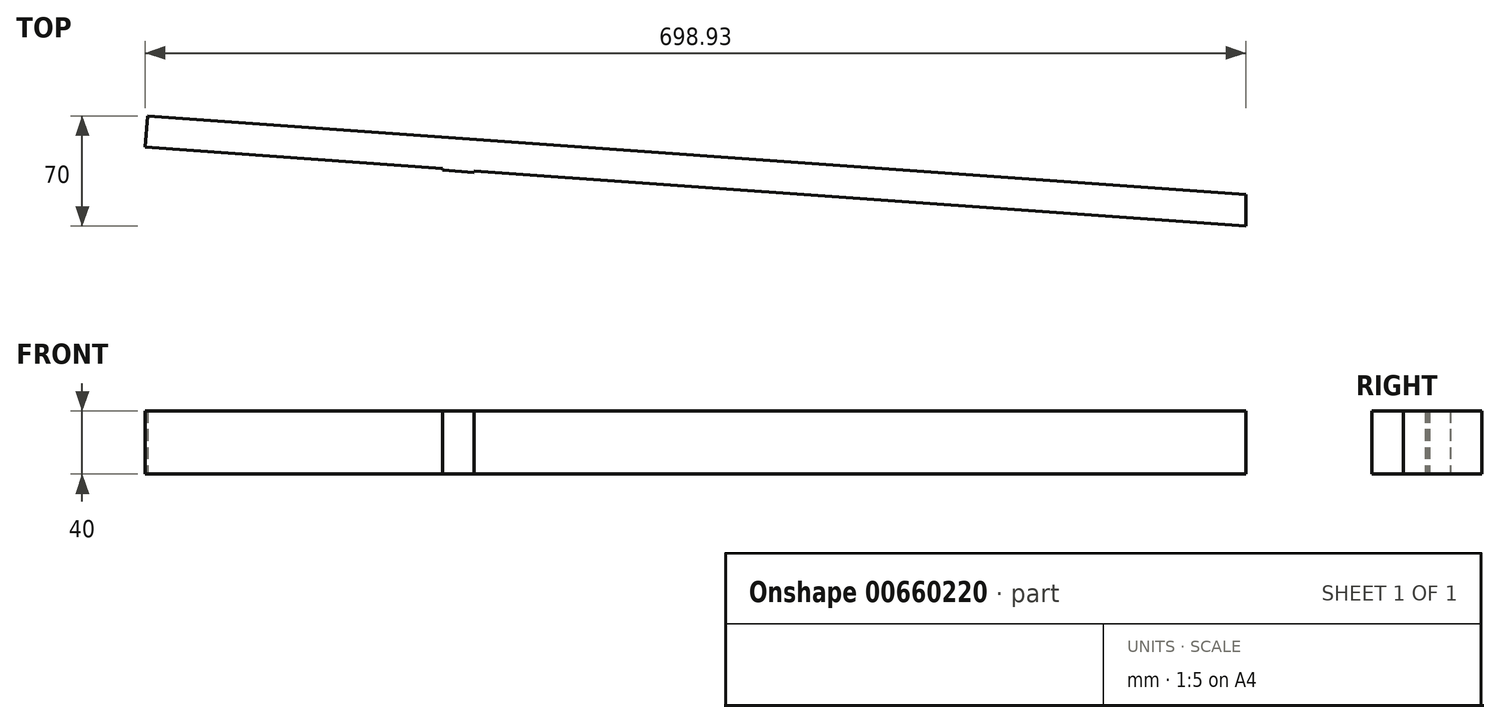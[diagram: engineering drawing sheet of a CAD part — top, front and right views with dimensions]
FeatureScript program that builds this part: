
annotation { "Feature Type Name" : "Feature", "Feature Type Description" : "" }
export const myFeature = defineFeature(function(context is Context, id is Id, definition is map)
    precondition{}
    {
        {
            var Q0;
            Q0=qCreatedBy(makeId("Top.planeOp"),FACE);
            var sketch = newSketch(context, id + "F0", { "sketchPlane" : qUnion([Q0])});
            skLineSegment(sketch, "E0", {"start": v(0, 0) * mm, "end": v(700, 0) * mm, "construction": true});
            skLineSegment(sketch, "E1", {"start": v(0, 0) * mm, "end": v(-698.21, 50) * mm, "construction": true});
            skLineSegment(sketch, "E2", {"start": v(-698.21, 50) * mm, "end": v(-697.5, 59.97) * mm});
            skLineSegment(sketch, "E3", {"start": v(-698.21, 50) * mm, "end": v(-698.93, 40.03) * mm});
            skLineSegment(sketch, "E4", {"start": v(-698.93, 40.03) * mm, "end": v(-510, 26.5) * mm});
            skLineSegment(sketch, "E5", {"start": v(-697.5, 59.97) * mm, "end": v(0, 10.03) * mm});
            skLineSegment(sketch, "E6.left", {"start": v(-510, 25.5) * mm, "end": v(-510, 26.5) * mm});
            skLineSegment(sketch, "E6.right", {"start": v(-490, 24.06) * mm, "end": v(-490, 25.06) * mm});
            skLineSegment(sketch, "E7.trimOffspring", {"start": v(-490, 25.06) * mm, "end": v(-0.36, -10) * mm});
            skLineSegment(sketch, "E8", {"start": v(0, 10.03) * mm, "end": v(0, -10.03) * mm});
            skLineSegment(sketch, "E9", {"start": v(-0.36, -10) * mm, "end": v(0, -10.03) * mm});
            skPoint(sketch, "E10.orphan", {"position": v(0, 10.82) * mm});
            skLineSegment(sketch, "E11", {"start": v(-510, 25.5) * mm, "end": v(-490, 24.06) * mm});
            skSolve(sketch);
        }
        {
            var Q0;
            Q0=qSketchRegion(id+"F0",true);
            extrude(context, id + "F1", {"entities" : qUnion([Q0]), "depth" : 40 * mm, "offsetDistance" : 25 * mm});
        }
    });
